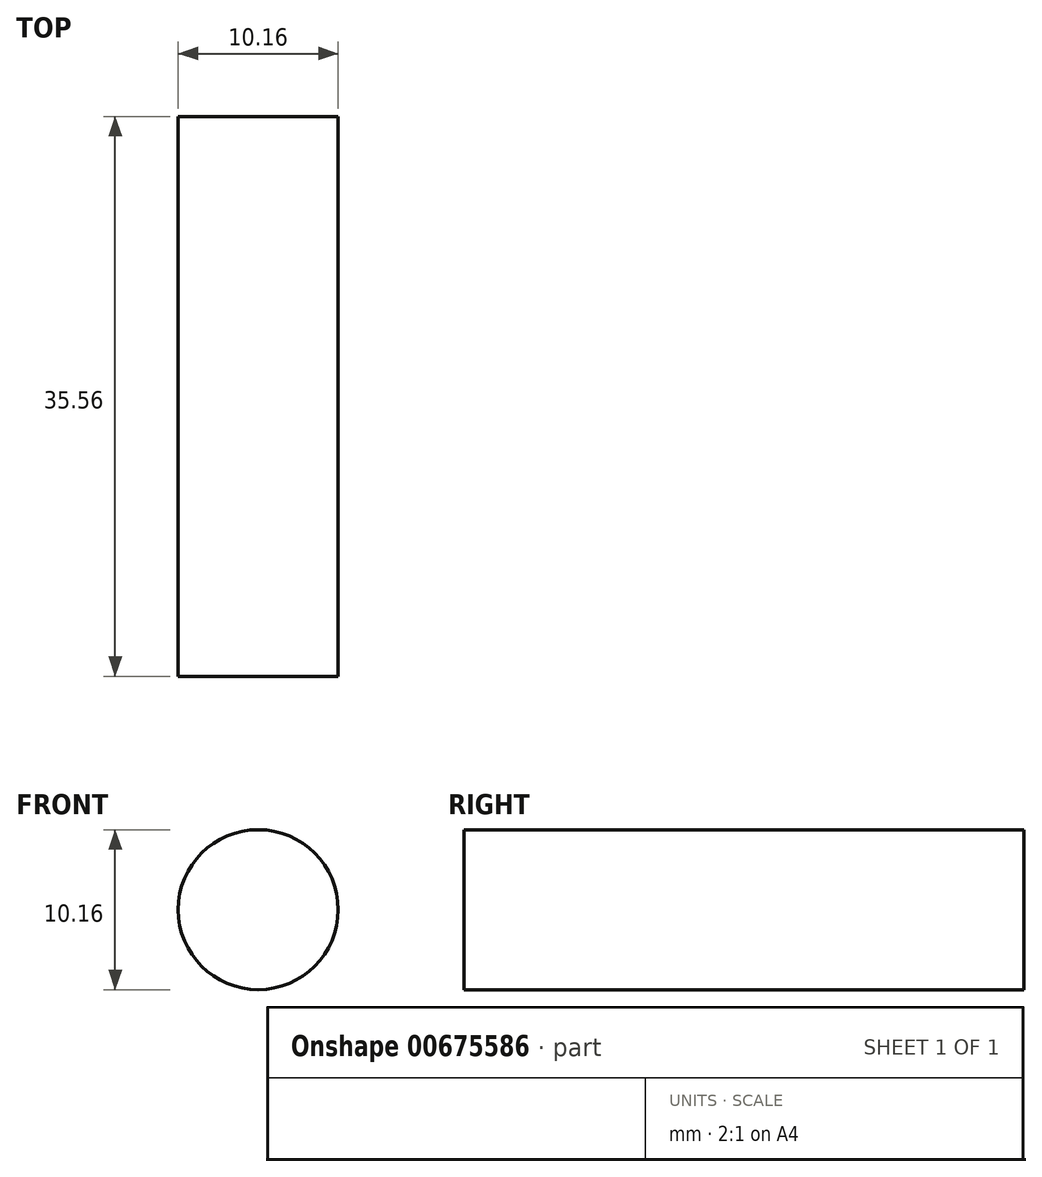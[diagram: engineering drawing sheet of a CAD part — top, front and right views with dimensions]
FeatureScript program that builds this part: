
annotation { "Feature Type Name" : "Feature", "Feature Type Description" : "" }
export const myFeature = defineFeature(function(context is Context, id is Id, definition is map)
    precondition{}
    {
        {
            var Q0;
            Q0=qCreatedBy(makeId("Front.planeOp"),FACE);
            var sketch = newSketch(context, id + "F0", { "sketchPlane" : qUnion([Q0])});
            skCircle(sketch, "E0", {"center": v(0, 0) * mm, "radius": 5.08 * mm});
            skSolve(sketch);
        }
        {
            var Q0;
            Q0 = qSketchRegion(id + "F0", true);
            extrude(context, id + "F1", {"entities" : qUnion([Q0]), "depth" : 35.56 * mm, "offsetDistance" : 25.4 * mm});
        }
    });
